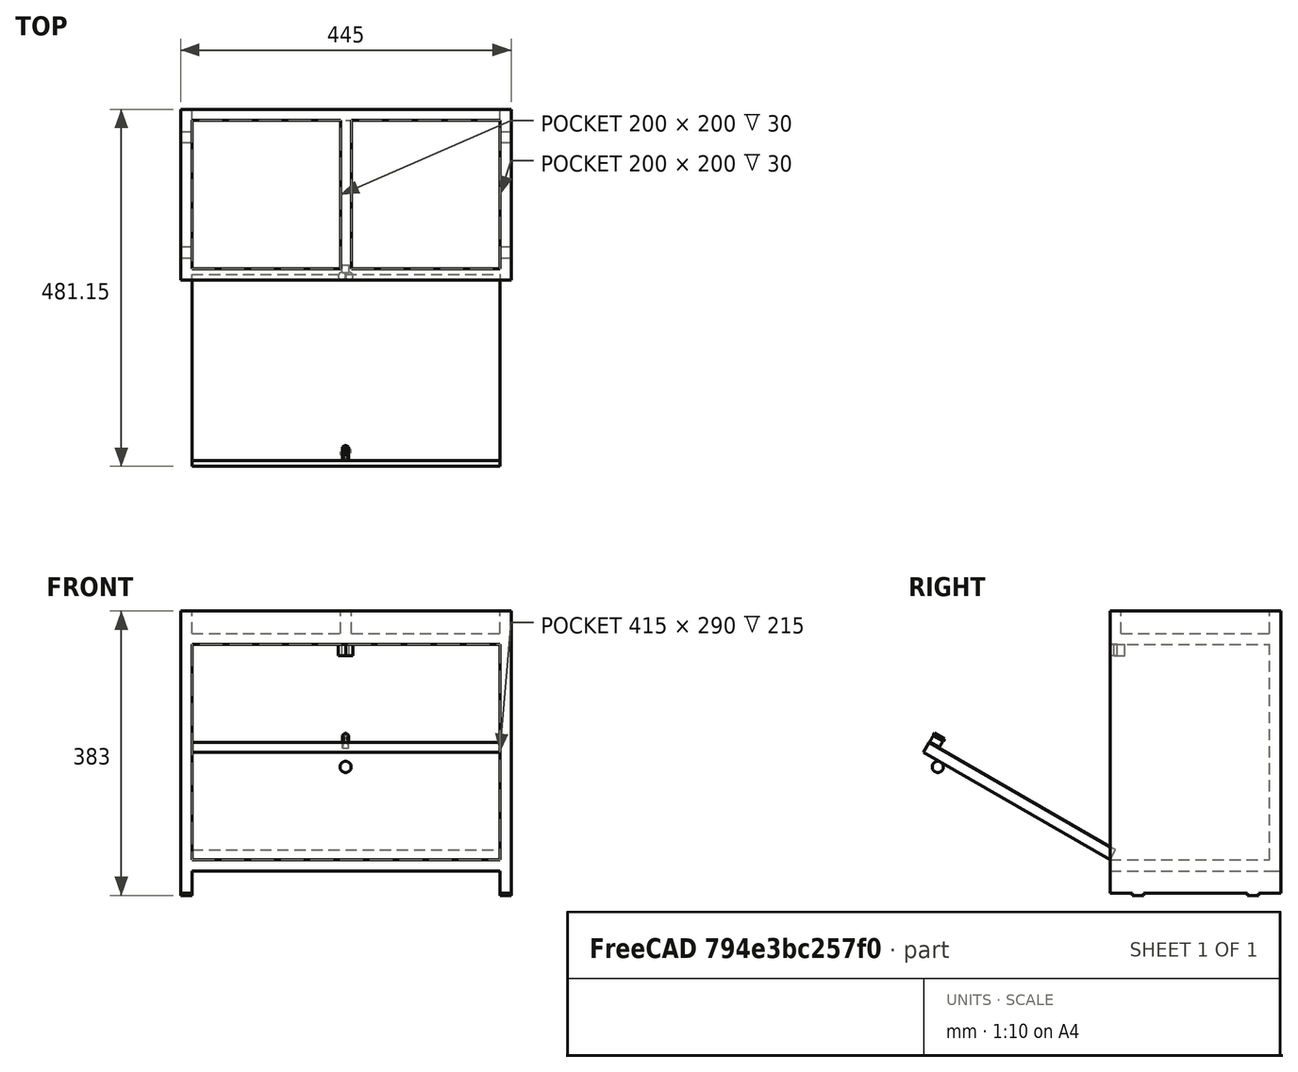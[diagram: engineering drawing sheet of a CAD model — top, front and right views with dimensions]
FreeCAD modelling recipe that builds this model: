
FCSTD DOCUMENT  (FreeCAD 0.17R13522 (Git))
Label: SuporteParaComedouroTamanho2Fusao
License: All rights reserved
LicenseURL: http://en.wikipedia.org/wiki/All_rights_reserved
objects: Part::Box×14, TechDraw::DrawViewDimension×14, Part::Cylinder×4, TechDraw::DrawViewPart×4, Part::MultiFuse×2, Part::Cut×2, Part::Sphere×1, Part::Chamfer×1, TechDraw::DrawSVGTemplate×1, TechDraw::DrawPage×1
note: 24 computed .brp shape members not serialized (recipe doc carries the construction recipe); baked Part::Feature solids carry a one-line shape summary decoded from their .brp

FEATURE [Part::Box] Box  label="SuporteFrenteSuperiorVertical"
  AttacherType = Attacher::AttachEngine3D
  Height = 30
  Length = 415
  Width = 15
FEATURE [Part::Box] Box001  label="SuporteLateralVerticalEsquerdo"
  AttacherType = Attacher::AttachEngine3D
  Height = 380
  Length = 15
  Placement = pos=(-15,0,-350) rot=(0,0,1;0rad)
  Width = 230
FEATURE [Part::Box] Box002  label="SuporteLateralVerticalDireito"
  AttacherType = Attacher::AttachEngine3D
  Height = 380
  Length = 15
  Placement = pos=(415,0,-350) rot=(0,0,1;0rad)
  Width = 230
FEATURE [Part::Box] Box003  label="TampoSuperiorHorizontal"
  AttacherType = Attacher::AttachEngine3D
  Height = 15
  Length = 415
  Placement = pos=(0,0,-15) rot=(0,0,1;0rad)
  Width = 215
FEATURE [Part::Box] Box004  label="SuporteFundoVertical"
  AttacherType = Attacher::AttachEngine3D
  Height = 350
  Length = 415
  Placement = pos=(0,215,-320) rot=(0,0,1;0rad)
  Width = 15
FEATURE [Part::Box] Box005  label="SuporteVerticalMeio"
  AttacherType = Attacher::AttachEngine3D
  Height = 30
  Length = 15
  Placement = pos=(200,15,0) rot=(0,0,1;0rad)
  Width = 200
FEATURE [Part::Box] Box006  label="TampoInferiorHorizontal"
  AttacherType = Attacher::AttachEngine3D
  Height = 15
  Length = 415
  Placement = pos=(0,0,-320) rot=(0,0,1;0rad)
  Width = 215
FEATURE [Part::Box] Box007  label="Cube"
  AttacherType = Attacher::AttachEngine3D
  Height = 3
  Length = 15
  Placement = pos=(-15,30,-353) rot=(0,0,1;0rad)
  Width = 15
FEATURE [Part::Box] Box008  label="Cube001"
  AttacherType = Attacher::AttachEngine3D
  Height = 3
  Length = 15
  Placement = pos=(-15,185,-353) rot=(0,0,1;0rad)
  Width = 15
FEATURE [Part::Box] Box009  label="Cube002"
  AttacherType = Attacher::AttachEngine3D
  Height = 3
  Length = 15
  Placement = pos=(415,30,-353) rot=(0,0,1;0rad)
  Width = 15
FEATURE [Part::Box] Box010  label="Cube003"
  AttacherType = Attacher::AttachEngine3D
  Height = 3
  Length = 15
  Placement = pos=(415,185,-353) rot=(0,0,1;0rad)
  Width = 15
FEATURE [Part::Box] Box011  label="TampaBasculante"
  AttacherType = Attacher::AttachEngine3D
  Height = 290
  Length = 415
  Placement = pos=(0,0,-305) rot=(1,0,0;1.0472rad)
  Width = 15
FEATURE [Part::Sphere] Sphere  label="Puxador"
  Angle1 = -90
  Angle2 = 90
  Angle3 = 360
  AttacherType = Attacher::AttachEngine3D
  Placement = pos=(207,-232,-180) rot=(0,0,1;0rad)
  Radius = 7.5
FEATURE [Part::Cylinder] Cylinder
  Angle = 360
  AttacherType = Attacher::AttachEngine3D
  Height = 15
  Placement = pos=(-100,0,0) rot=(0,0,1;0rad)
  Radius = 5
FEATURE [Part::Cylinder] Cylinder001
  Angle = 360
  AttacherType = Attacher::AttachEngine3D
  Height = 15
  Placement = pos=(-90,0,0) rot=(0,0,1;0rad)
  Radius = 5
FEATURE [Part::Box] Box012  label="Cube004"
  AttacherType = Attacher::AttachEngine3D
  Height = 15
  Length = 10
  Placement = pos=(-100,5,0) rot=(0,0,1;0rad)
  Width = 10
FEATURE [Part::MultiFuse] Fusion
  Placement = pos=(302,5,-30) rot=(0,0,1;0rad)
  Shapes = -> [Cylinder,Cylinder001,Box012]
FEATURE [Part::Box] Box013  label="Cube005"
  AttacherType = Attacher::AttachEngine3D
  Height = 15
  Length = 8
  Placement = pos=(193,-130,-70) rot=(0,0,1;0rad)
  Width = 15
FEATURE [Part::Chamfer] Chamfer
  Base = -> Box013
  Edges = 2 edges r=3.9: [Edge3,Edge7]
FEATURE [Part::Cylinder] Cylinder002
  Angle = 360
  AttacherType = Attacher::AttachEngine3D
  Height = 15
  Placement = pos=(212,-124,-70) rot=(0,0,1;0rad)
  Radius = 12
FEATURE [Part::Cylinder] Cylinder003
  Angle = 360
  AttacherType = Attacher::AttachEngine3D
  Height = 15
  Placement = pos=(182,-124,-70) rot=(0,0,1;0rad)
  Radius = 12
FEATURE [Part::Cut] Cut
  Base = -> Chamfer
  Tool = -> Cylinder002
FEATURE [Part::Cut] Cut001
  Base = -> Cut
  Placement = pos=(10,-226,-7) rot=(1,0,0;1.0472rad)
  Tool = -> Cylinder003
FEATURE [Part::MultiFuse] Fusion001
  Shapes = -> [Box,Box001,Box002,Box003,Box004,Box005,Box006,Box007,Box008,Box009,Box010,Box011,Sphere,Fusion,Cut001]
FEATURE [TechDraw::DrawSVGTemplate] Template
  EditableTexts = AUTHOR_NAME=Sérgio C. G. Alves; DN=DN; DRAWING_TITLE=Tamanho 2; FC-DATE=25/05/2018; FC-REV=REV A; FC-SC=SCALE; FC-SH=X / Y; FC-SI=A3; FreeCAD_DRAWING=Material: Pinho; PN=PN
  Height = 297
  Orientation = 1
  Width = 420
FEATURE [TechDraw::DrawViewPart] View  label="Superior"
  CoarseView = false
  Direction = (0,0,1)
  Focus = 100
  HardHidden = false
  IsoCount = 0
  IsoHidden = false
  IsoVisible = false
  LockPosition = false
  Perspective = false
  Rotation = 0
  Scale = 0.2
  ScaleType = 2
  SeamHidden = false
  SeamVisible = false
  SmoothHidden = false
  SmoothVisible = false
  Source = -> [Fusion001]
  X = 345.487
  Y = 217.666
FEATURE [TechDraw::DrawViewPart] View001  label="Lateral"
  CoarseView = false
  Direction = (1,0,0)
  Focus = 100
  HardHidden = false
  IsoCount = 0
  IsoHidden = false
  IsoVisible = false
  LockPosition = false
  Perspective = false
  Rotation = 0
  Scale = 0.2
  ScaleType = 2
  SeamHidden = false
  SeamVisible = false
  SmoothHidden = false
  SmoothVisible = false
  Source = -> [Fusion001]
  X = 79.8679
  Y = 66.3113
FEATURE [TechDraw::DrawViewDimension] Dimension
  FormatSpec = %.2f
  LockPosition = false
  MeasureType = 1
  References2D = -> [View]
  Rotation = 0
  Scale = 0.2
  ScaleType = 0
  Type = 1
  X = 0.347536
  Y = 57.5171
FEATURE [TechDraw::DrawViewDimension] Dimension001
  FormatSpec = %.2f
  LockPosition = false
  MeasureType = 1
  References2D = -> [View]
  Rotation = 0
  Scale = 0.2
  ScaleType = 0
  Type = 1
  X = 0.521303
  Y = 63.7728
FEATURE [TechDraw::DrawViewDimension] Dimension002
  FormatSpec = %.2f
  LockPosition = false
  MeasureType = 1
  References2D = -> [View]
  Rotation = 0
  Scale = 0.2
  ScaleType = 0
  Type = 2
  X = 47.6124
  Y = 25.0226
FEATURE [TechDraw::DrawViewDimension] Dimension003
  FormatSpec = %.2f
  LockPosition = false
  MeasureType = 1
  References2D = -> [View]
  Rotation = 0
  Scale = 0.2
  ScaleType = 0
  Type = 2
  X = 54.0418
  Y = 25.0226
FEATURE [TechDraw::DrawViewDimension] Dimension004
  FormatSpec = %.2f
  LockPosition = false
  MeasureType = 1
  References2D = -> [View]
  Rotation = 0
  Scale = 0.2
  ScaleType = 0
  Type = 1
  X = -19.2257
  Y = -1.52283
FEATURE [TechDraw::DrawViewDimension] Dimension005
  FormatSpec = %.2f
  LockPosition = false
  MeasureType = 1
  References2D = -> [View001]
  Rotation = 0
  Scale = 0.2
  ScaleType = 0
  Type = 1
  X = 25.7732
  Y = 49.0442
FEATURE [TechDraw::DrawViewDimension] Dimension006
  FormatSpec = %.2f
  LockPosition = false
  MeasureType = 1
  References2D = -> [View001]
  Rotation = 0
  Scale = 0.2
  ScaleType = 0
  Type = 2
  X = 51.5465
  Y = 2.75248
FEATURE [TechDraw::DrawViewDimension] Dimension007
  FormatSpec = %.2f
  LockPosition = false
  MeasureType = 1
  References2D = -> [View001]
  Rotation = 0
  Scale = 0.2
  ScaleType = 0
  Type = 2
  X = -22.0199
  Y = -39.7859
FEATURE [TechDraw::DrawViewPart] View002  label="Frente"
  CoarseView = false
  Direction = (0,-1,0)
  Focus = 100
  HardHidden = false
  IsoCount = 0
  IsoHidden = false
  IsoVisible = false
  LockPosition = false
  Perspective = false
  Rotation = 0
  Scale = 0.2
  ScaleType = 2
  SeamHidden = false
  SeamVisible = false
  SmoothHidden = false
  SmoothVisible = false
  Source = -> [Fusion001]
  X = 210
  Y = 148.5
FEATURE [TechDraw::DrawViewDimension] Dimension008
  FormatSpec = %.2f
  LockPosition = false
  MeasureType = 1
  References2D = -> [View002]
  Rotation = 0
  Scale = 0.2
  ScaleType = 0
  Type = 2
  X = -23.98
  Y = -47.3344
FEATURE [TechDraw::DrawViewDimension] Dimension009
  FormatSpec = %.2f
  LockPosition = false
  MeasureType = 1
  References2D = -> [View002]
  Rotation = 0
  Scale = 0.2
  ScaleType = 0
  Type = 2
  X = 48.0642
  Y = 48.3814
FEATURE [TechDraw::DrawViewDimension] Dimension010
  FormatSpec = %.2f
  LockPosition = false
  MeasureType = 1
  References2D = -> [View002]
  Rotation = 0
  Scale = 0.2
  ScaleType = 0
  Type = 2
  X = 52.0298
  Y = 1.90353
FEATURE [TechDraw::DrawViewDimension] Dimension011
  FormatSpec = %.2f
  LockPosition = false
  MeasureType = 1
  References2D = -> [View002]
  Rotation = 0
  Scale = 0.2
  ScaleType = 0
  Type = 2
  X = -54.441
  Y = 1.90353
FEATURE [TechDraw::DrawViewDimension] Dimension012
  FormatSpec = %.2f
  LockPosition = false
  MeasureType = 1
  References2D = -> [View002]
  Rotation = 0
  Scale = 0.2
  ScaleType = 0
  Type = 1
  X = 0.250226
  Y = 48.5438
FEATURE [TechDraw::DrawViewDimension] Dimension013
  FormatSpec = %.2f
  LockPosition = false
  MeasureType = 1
  References2D = -> [View002]
  Rotation = 0
  Scale = 0.2
  ScaleType = 0
  Type = 1
  X = 0.750677
  Y = 55.0496
FEATURE [TechDraw::DrawViewPart] View003  label="Perspectiva"
  CoarseView = false
  Direction = (1,-1,1)
  Focus = 100
  HardHidden = false
  IsoCount = 0
  IsoHidden = false
  IsoVisible = false
  LockPosition = false
  Perspective = false
  Rotation = 0
  Scale = 0.15
  ScaleType = 0
  SeamHidden = false
  SeamVisible = false
  SmoothHidden = false
  SmoothVisible = false
  Source = -> [Fusion001]
  X = 82.453
  Y = 231.712
FEATURE [TechDraw::DrawPage] Page
  KeepUpdated = true
  ProjectionType = 0
  Scale = 0.2
  Template = -> Template
  Views = -> [View,View001,Dimension,Dimension001,Dimension002,Dimension003,Dimension004,Dimension005,Dimension006,Dimension007,View002,Dimension008,Dimension009,Dimension010,Dimension011,Dimension012,Dimension013,View003]
